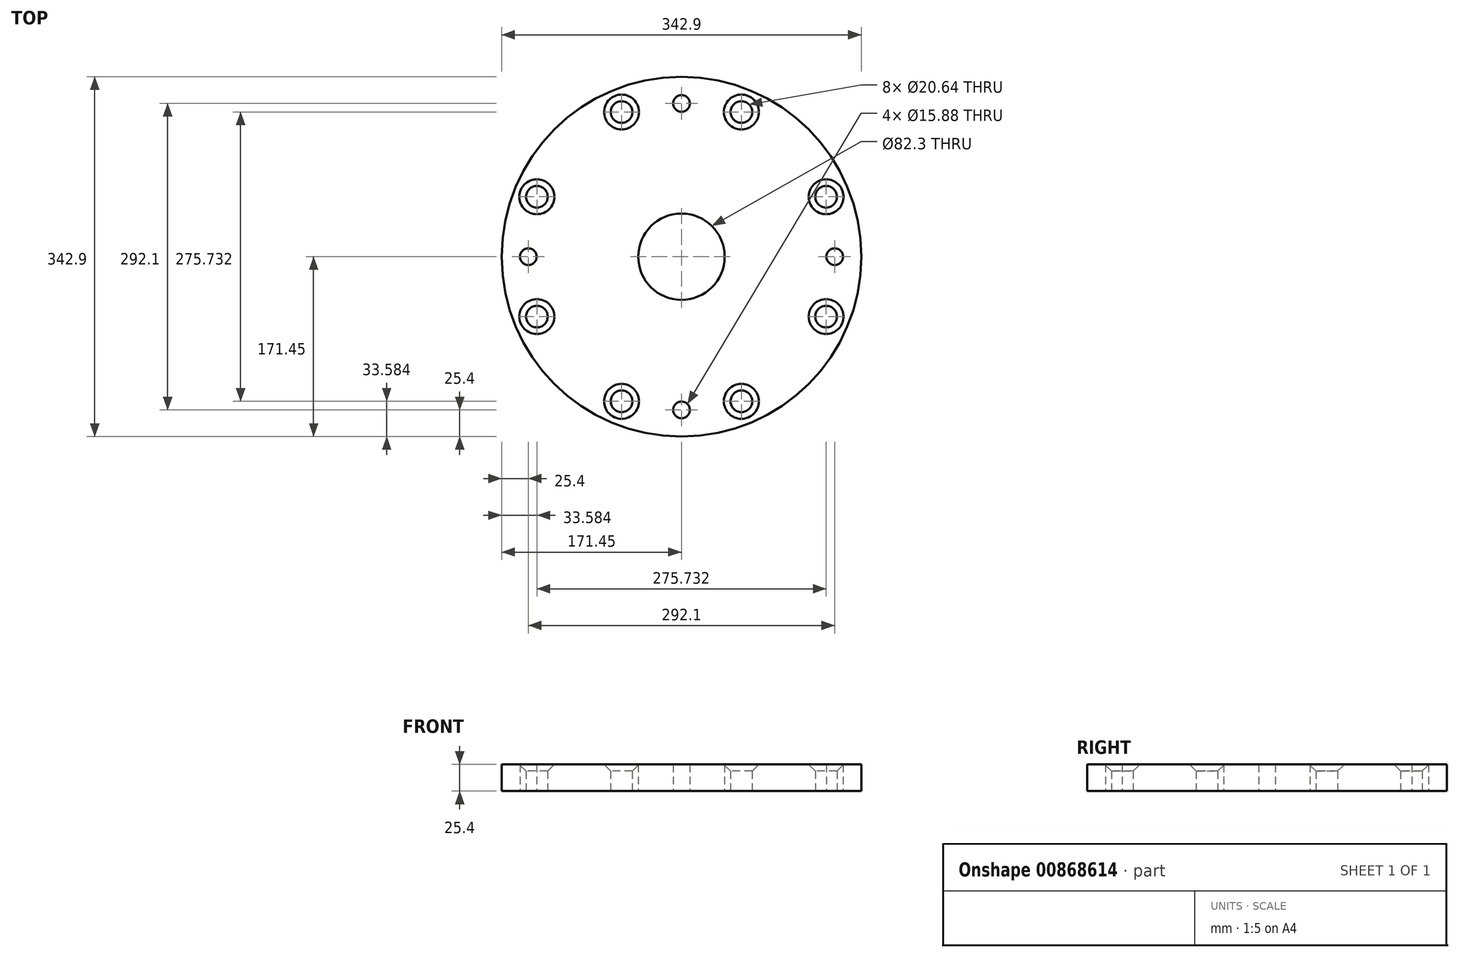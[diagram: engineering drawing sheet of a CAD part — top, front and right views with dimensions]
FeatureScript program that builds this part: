
annotation { "Feature Type Name" : "Feature", "Feature Type Description" : "" }
export const myFeature = defineFeature(function(context is Context, id is Id, definition is map)
    precondition{}
    {
        {
            var Q0;
            Q0=qCreatedBy(makeId("Top.planeOp"),FACE);
            var sketch = newSketch(context, id + "F0", { "sketchPlane" : qUnion([Q0])});
            skCircle(sketch, "E0", {"center": v(0, 0) * mm, "radius": 171.45 * mm});
            skCircle(sketch, "E1", {"center": v(0, 0) * mm, "radius": 146.05 * mm});
            skCircle(sketch, "E2", {"center": v(-146.05, 0) * mm, "radius": 7.94 * mm});
            skCircle(sketch, "E3", {"center": v(146.05, 0) * mm, "radius": 7.94 * mm});
            skCircle(sketch, "E4", {"center": v(0, 146.05) * mm, "radius": 7.94 * mm});
            skCircle(sketch, "E5", {"center": v(0, -146.05) * mm, "radius": 7.94 * mm});
            skCircle(sketch, "E6", {"center": v(0, 0) * mm, "radius": 149.23 * mm});
            skLineSegment(sketch, "E7", {"start": v(0, 0) * mm, "end": v(239, 0) * mm});
            skLineSegment(sketch, "E8", {"start": v(0, 0) * mm, "end": v(224.7, 93.07) * mm});
            skLineSegment(sketch, "E9", {"start": v(0, 0) * mm, "end": v(82.7, 199.64) * mm});
            skLineSegment(sketch, "E10.MirrorCS", {"start": v(0, 0) * mm, "end": v(-82.7, 199.64) * mm});
            skLineSegment(sketch, "E11.MirrorCS", {"start": v(0, 0) * mm, "end": v(-224.7, 93.07) * mm});
            skLineSegment(sketch, "E12.MirrorCS", {"start": v(0, 0) * mm, "end": v(224.7, -93.07) * mm});
            skLineSegment(sketch, "E13.MirrorCS", {"start": v(0, 0) * mm, "end": v(82.7, -199.64) * mm});
            skLineSegment(sketch, "E14.MirrorCS", {"start": v(0, 0) * mm, "end": v(-82.7, -199.64) * mm});
            skLineSegment(sketch, "E15.MirrorCS", {"start": v(0, 0) * mm, "end": v(-224.7, -93.07) * mm});
            skCircle(sketch, "E16", {"center": v(137.87, 57.1) * mm, "radius": 10.32 * mm});
            skCircle(sketch, "E17", {"center": v(57.1, 137.87) * mm, "radius": 10.32 * mm});
            skCircle(sketch, "E18", {"center": v(-57.1, 137.87) * mm, "radius": 10.32 * mm});
            skCircle(sketch, "E19", {"center": v(-137.87, 57.1) * mm, "radius": 10.32 * mm});
            skCircle(sketch, "E20", {"center": v(137.87, -57.1) * mm, "radius": 10.32 * mm});
            skCircle(sketch, "E21", {"center": v(57.1, -137.87) * mm, "radius": 10.32 * mm});
            skCircle(sketch, "E22", {"center": v(-57.1, -137.87) * mm, "radius": 10.32 * mm});
            skCircle(sketch, "E23", {"center": v(-137.87, -57.1) * mm, "radius": 10.32 * mm});
            skCircle(sketch, "E24", {"center": v(0, 0) * mm, "radius": 41.15 * mm});
            skSolve(sketch);
        }
        {
            var Q0;
            {var subQ1=sQuery(id+"F0.wireOp",EDGE,"E0");var subQ9=sQuery(id+"F0.wireOp",EDGE,"E8");var subQ10=makeQuery(id+"F0.imprint","INTERSECT",VERTEX,{"derivedFrom":[subQ1,subQ9]});Q0=makeQuery(id+"F0.imprint","IMPRINT",FACE,{"disambiguationData":[TD([[makeQuery(id+"F0.imprint","IMPRINT",EDGE,{"disambiguationData":[TD([[subQ10,1.0]])],"derivedFrom":subQ1}),1.0]])]});}
            var Q1;
            {var subQ1=sQuery(id+"F0.wireOp",EDGE,"E0");var subQ5=sQuery(id+"F0.wireOp",EDGE,"E8");var subQ6=makeQuery(id+"F0.imprint","INTERSECT",VERTEX,{"derivedFrom":[subQ1,subQ5]});Q1=makeQuery(id+"F0.imprint","IMPRINT",FACE,{"disambiguationData":[TD([[makeQuery(id+"F0.imprint","IMPRINT",EDGE,{"disambiguationData":[TD([[subQ6,-1.0]])],"derivedFrom":subQ1}),1.0]])]});}
            var Q2;
            {var subQ0=sQuery(id+"F0.wireOp",EDGE,"E10.MirrorCS");var subQ1=sQuery(id+"F0.wireOp",EDGE,"E0");var subQ2=makeQuery(id+"F0.imprint","INTERSECT",VERTEX,{"derivedFrom":[subQ1,subQ0]});Q2=makeQuery(id+"F0.imprint","IMPRINT",FACE,{"disambiguationData":[TD([[makeQuery(id+"F0.imprint","IMPRINT",EDGE,{"disambiguationData":[TD([[subQ2,-1.0]])],"derivedFrom":subQ1}),1.0]])]});}
            var Q3;
            {var subQ0=sQuery(id+"F0.wireOp",EDGE,"E13.MirrorCS");var subQ1=sQuery(id+"F0.wireOp",EDGE,"E0");var subQ2=makeQuery(id+"F0.imprint","INTERSECT",VERTEX,{"derivedFrom":[subQ1,subQ0]});Q3=makeQuery(id+"F0.imprint","IMPRINT",FACE,{"disambiguationData":[TD([[makeQuery(id+"F0.imprint","IMPRINT",EDGE,{"disambiguationData":[TD([[subQ2,-1.0]])],"derivedFrom":subQ1}),1.0]])]});}
            var Q4;
            {var subQ5=sQuery(id+"F0.wireOp",EDGE,"E7");var subQ8=sQuery(id+"F0.wireOp",EDGE,"E0");var subQ11=makeQuery(id+"F0.imprint","INTERSECT",VERTEX,{"derivedFrom":[subQ8,subQ5]});Q4=makeQuery(id+"F0.imprint","IMPRINT",FACE,{"disambiguationData":[TD([[makeQuery(id+"F0.imprint","IMPRINT",EDGE,{"disambiguationData":[TD([[subQ11,1.0]])],"derivedFrom":subQ8}),1.0]])]});}
            var Q5;
            {var subQ8=sQuery(id+"F0.wireOp",EDGE,"E9");var subQ9=sQuery(id+"F0.wireOp",EDGE,"E0");var subQ10=makeQuery(id+"F0.imprint","INTERSECT",VERTEX,{"derivedFrom":[subQ9,subQ8]});Q5=makeQuery(id+"F0.imprint","IMPRINT",FACE,{"disambiguationData":[TD([[makeQuery(id+"F0.imprint","IMPRINT",EDGE,{"disambiguationData":[TD([[subQ10,-1.0]])],"derivedFrom":subQ9}),1.0]])]});}
            var Q6;
            {var subQ5=sQuery(id+"F0.wireOp",EDGE,"E14.MirrorCS");var subQ6=sQuery(id+"F0.wireOp",EDGE,"E0");var subQ7=makeQuery(id+"F0.imprint","INTERSECT",VERTEX,{"derivedFrom":[subQ6,subQ5]});Q6=makeQuery(id+"F0.imprint","IMPRINT",FACE,{"disambiguationData":[TD([[makeQuery(id+"F0.imprint","IMPRINT",EDGE,{"disambiguationData":[TD([[subQ7,-1.0]])],"derivedFrom":subQ6}),1.0]])]});}
            var Q7;
            {var subQ8=sQuery(id+"F0.wireOp",EDGE,"E11.MirrorCS");var subQ9=sQuery(id+"F0.wireOp",EDGE,"E0");var subQ10=makeQuery(id+"F0.imprint","INTERSECT",VERTEX,{"derivedFrom":[subQ9,subQ8]});Q7=makeQuery(id+"F0.imprint","IMPRINT",FACE,{"disambiguationData":[TD([[makeQuery(id+"F0.imprint","IMPRINT",EDGE,{"disambiguationData":[TD([[subQ10,-1.0]])],"derivedFrom":subQ9}),1.0]])]});}
            var Q8;
            {var subQ3=sQuery(id+"F0.wireOp",EDGE,"E19");var subQ6=sQuery(id+"F0.wireOp",EDGE,"E1");var subQ13=makeQuery(id+"F0.imprint","INTERSECT",VERTEX,{"disambiguationData":[OD(1.0)],"derivedFrom":[subQ6,subQ3]});Q8=makeQuery(id+"F0.imprint","IMPRINT",FACE,{"disambiguationData":[TD([[makeQuery(id+"F0.imprint","IMPRINT",EDGE,{"disambiguationData":[TD([[subQ13,-1.0]])],"derivedFrom":subQ6}),1.0]])]});}
            var Q9;
            {var subQ0=sQuery(id+"F0.wireOp",EDGE,"E18");var subQ1=sQuery(id+"F0.wireOp",EDGE,"E1");var subQ2=makeQuery(id+"F0.imprint","INTERSECT",VERTEX,{"disambiguationData":[OD(1.0)],"derivedFrom":[subQ1,subQ0]});Q9=makeQuery(id+"F0.imprint","IMPRINT",FACE,{"disambiguationData":[TD([[makeQuery(id+"F0.imprint","IMPRINT",EDGE,{"disambiguationData":[TD([[subQ2,-1.0]])],"derivedFrom":subQ1}),1.0]])]});}
            var Q10;
            {var subQ1=sQuery(id+"F0.wireOp",EDGE,"E1");var subQ12=sQuery(id+"F0.wireOp",EDGE,"E17");var subQ14=makeQuery(id+"F0.imprint","INTERSECT",VERTEX,{"disambiguationData":[OD(1.0)],"derivedFrom":[subQ1,subQ12]});Q10=makeQuery(id+"F0.imprint","IMPRINT",FACE,{"disambiguationData":[TD([[makeQuery(id+"F0.imprint","IMPRINT",EDGE,{"disambiguationData":[TD([[subQ14,-1.0]])],"derivedFrom":subQ1}),1.0]])]});}
            var Q11;
            {var subQ0=sQuery(id+"F0.wireOp",EDGE,"E16");var subQ1=sQuery(id+"F0.wireOp",EDGE,"E1");var subQ2=makeQuery(id+"F0.imprint","INTERSECT",VERTEX,{"disambiguationData":[OD(1.0)],"derivedFrom":[subQ1,subQ0]});Q11=makeQuery(id+"F0.imprint","IMPRINT",FACE,{"disambiguationData":[TD([[makeQuery(id+"F0.imprint","IMPRINT",EDGE,{"disambiguationData":[TD([[subQ2,-1.0]])],"derivedFrom":subQ1}),1.0]])]});}
            var Q12;
            {var subQ1=sQuery(id+"F0.wireOp",EDGE,"E3");var subQ5=sQuery(id+"F0.wireOp",EDGE,"E1");var subQ6=makeQuery(id+"F0.imprint","INTERSECT",VERTEX,{"disambiguationData":[OD(0.0)],"derivedFrom":[subQ5,subQ1]});Q12=makeQuery(id+"F0.imprint","IMPRINT",FACE,{"disambiguationData":[TD([[makeQuery(id+"F0.imprint","IMPRINT",EDGE,{"disambiguationData":[TD([[subQ6,-1.0]])],"derivedFrom":subQ5}),1.0]])]});}
            var Q13;
            {var subQ3=sQuery(id+"F0.wireOp",EDGE,"E20");var subQ9=sQuery(id+"F0.wireOp",EDGE,"E1");var subQ11=makeQuery(id+"F0.imprint","INTERSECT",VERTEX,{"disambiguationData":[OD(1.0)],"derivedFrom":[subQ9,subQ3]});Q13=makeQuery(id+"F0.imprint","IMPRINT",FACE,{"disambiguationData":[TD([[makeQuery(id+"F0.imprint","IMPRINT",EDGE,{"disambiguationData":[TD([[subQ11,-1.0]])],"derivedFrom":subQ9}),1.0]])]});}
            var Q14;
            {var subQ1=sQuery(id+"F0.wireOp",EDGE,"E1");var subQ8=sQuery(id+"F0.wireOp",EDGE,"E21");var subQ11=makeQuery(id+"F0.imprint","INTERSECT",VERTEX,{"disambiguationData":[OD(1.0)],"derivedFrom":[subQ1,subQ8]});Q14=makeQuery(id+"F0.imprint","IMPRINT",FACE,{"disambiguationData":[TD([[makeQuery(id+"F0.imprint","IMPRINT",EDGE,{"disambiguationData":[TD([[subQ11,-1.0]])],"derivedFrom":subQ1}),1.0]])]});}
            var Q15;
            {var subQ6=sQuery(id+"F0.wireOp",EDGE,"E1");var subQ10=sQuery(id+"F0.wireOp",EDGE,"E22");var subQ11=makeQuery(id+"F0.imprint","INTERSECT",VERTEX,{"disambiguationData":[OD(1.0)],"derivedFrom":[subQ6,subQ10]});Q15=makeQuery(id+"F0.imprint","IMPRINT",FACE,{"disambiguationData":[TD([[makeQuery(id+"F0.imprint","IMPRINT",EDGE,{"disambiguationData":[TD([[subQ11,-1.0]])],"derivedFrom":subQ6}),1.0]])]});}
            var Q16;
            {var subQ1=sQuery(id+"F0.wireOp",EDGE,"E1");var subQ5=sQuery(id+"F0.wireOp",EDGE,"E23");var subQ6=makeQuery(id+"F0.imprint","INTERSECT",VERTEX,{"disambiguationData":[OD(1.0)],"derivedFrom":[subQ1,subQ5]});Q16=makeQuery(id+"F0.imprint","IMPRINT",FACE,{"disambiguationData":[TD([[makeQuery(id+"F0.imprint","IMPRINT",EDGE,{"disambiguationData":[TD([[subQ6,-1.0]])],"derivedFrom":subQ1}),1.0]])]});}
            var Q17;
            {var subQ0=sQuery(id+"F0.wireOp",EDGE,"E2");var subQ1=sQuery(id+"F0.wireOp",EDGE,"E1");var subQ2=makeQuery(id+"F0.imprint","INTERSECT",VERTEX,{"disambiguationData":[OD(1.0)],"derivedFrom":[subQ1,subQ0]});Q17=makeQuery(id+"F0.imprint","IMPRINT",FACE,{"disambiguationData":[TD([[makeQuery(id+"F0.imprint","IMPRINT",EDGE,{"disambiguationData":[TD([[subQ2,-1.0]])],"derivedFrom":subQ1}),-1.0]])]});}
            var Q18;
            {var subQ0=sQuery(id+"F0.wireOp",EDGE,"E19");var subQ1=sQuery(id+"F0.wireOp",EDGE,"E1");var subQ2=makeQuery(id+"F0.imprint","INTERSECT",VERTEX,{"disambiguationData":[OD(1.0)],"derivedFrom":[subQ1,subQ0]});Q18=makeQuery(id+"F0.imprint","IMPRINT",FACE,{"disambiguationData":[TD([[makeQuery(id+"F0.imprint","IMPRINT",EDGE,{"disambiguationData":[TD([[subQ2,-1.0]])],"derivedFrom":subQ1}),-1.0]])]});}
            var Q19;
            {var subQ0=sQuery(id+"F0.wireOp",EDGE,"E15.MirrorCS");var subQ1=sQuery(id+"F0.wireOp",EDGE,"E0");var subQ2=makeQuery(id+"F0.imprint","INTERSECT",VERTEX,{"derivedFrom":[subQ1,subQ0]});Q19=makeQuery(id+"F0.imprint","IMPRINT",FACE,{"disambiguationData":[TD([[makeQuery(id+"F0.imprint","IMPRINT",EDGE,{"disambiguationData":[TD([[subQ2,-1.0]])],"derivedFrom":subQ1}),1.0]])]});}
            var Q20;
            {var subQ0=sQuery(id+"F0.wireOp",EDGE,"E23");var subQ1=sQuery(id+"F0.wireOp",EDGE,"E1");var subQ2=makeQuery(id+"F0.imprint","INTERSECT",VERTEX,{"disambiguationData":[OD(1.0)],"derivedFrom":[subQ1,subQ0]});Q20=makeQuery(id+"F0.imprint","IMPRINT",FACE,{"disambiguationData":[TD([[makeQuery(id+"F0.imprint","IMPRINT",EDGE,{"disambiguationData":[TD([[subQ2,-1.0]])],"derivedFrom":subQ1}),-1.0]])]});}
            var Q21;
            {var subQ0=sQuery(id+"F0.wireOp",EDGE,"E22");var subQ1=sQuery(id+"F0.wireOp",EDGE,"E1");var subQ2=makeQuery(id+"F0.imprint","INTERSECT",VERTEX,{"disambiguationData":[OD(1.0)],"derivedFrom":[subQ1,subQ0]});Q21=makeQuery(id+"F0.imprint","IMPRINT",FACE,{"disambiguationData":[TD([[makeQuery(id+"F0.imprint","IMPRINT",EDGE,{"disambiguationData":[TD([[subQ2,-1.0]])],"derivedFrom":subQ1}),-1.0]])]});}
            var Q22;
            {var subQ0=sQuery(id+"F0.wireOp",EDGE,"E5");var subQ1=sQuery(id+"F0.wireOp",EDGE,"E1");var subQ2=makeQuery(id+"F0.imprint","INTERSECT",VERTEX,{"disambiguationData":[OD(1.0)],"derivedFrom":[subQ1,subQ0]});Q22=makeQuery(id+"F0.imprint","IMPRINT",FACE,{"disambiguationData":[TD([[makeQuery(id+"F0.imprint","IMPRINT",EDGE,{"disambiguationData":[TD([[subQ2,-1.0]])],"derivedFrom":subQ1}),-1.0]])]});}
            var Q23;
            {var subQ0=sQuery(id+"F0.wireOp",EDGE,"E21");var subQ1=sQuery(id+"F0.wireOp",EDGE,"E1");var subQ2=makeQuery(id+"F0.imprint","INTERSECT",VERTEX,{"disambiguationData":[OD(1.0)],"derivedFrom":[subQ1,subQ0]});Q23=makeQuery(id+"F0.imprint","IMPRINT",FACE,{"disambiguationData":[TD([[makeQuery(id+"F0.imprint","IMPRINT",EDGE,{"disambiguationData":[TD([[subQ2,-1.0]])],"derivedFrom":subQ1}),-1.0]])]});}
            var Q24;
            {var subQ0=sQuery(id+"F0.wireOp",EDGE,"E20");var subQ1=sQuery(id+"F0.wireOp",EDGE,"E1");var subQ2=makeQuery(id+"F0.imprint","INTERSECT",VERTEX,{"disambiguationData":[OD(1.0)],"derivedFrom":[subQ1,subQ0]});Q24=makeQuery(id+"F0.imprint","IMPRINT",FACE,{"disambiguationData":[TD([[makeQuery(id+"F0.imprint","IMPRINT",EDGE,{"disambiguationData":[TD([[subQ2,-1.0]])],"derivedFrom":subQ1}),-1.0]])]});}
            var Q25;
            {var subQ0=sQuery(id+"F0.wireOp",EDGE,"E3");var subQ1=sQuery(id+"F0.wireOp",EDGE,"E1");var subQ2=makeQuery(id+"F0.imprint","INTERSECT",VERTEX,{"disambiguationData":[OD(0.0)],"derivedFrom":[subQ1,subQ0]});Q25=makeQuery(id+"F0.imprint","IMPRINT",FACE,{"disambiguationData":[TD([[makeQuery(id+"F0.imprint","IMPRINT",EDGE,{"disambiguationData":[TD([[subQ2,-1.0]])],"derivedFrom":subQ1}),-1.0]])]});}
            var Q26;
            {var subQ0=sQuery(id+"F0.wireOp",EDGE,"E16");var subQ1=sQuery(id+"F0.wireOp",EDGE,"E1");var subQ2=makeQuery(id+"F0.imprint","INTERSECT",VERTEX,{"disambiguationData":[OD(1.0)],"derivedFrom":[subQ1,subQ0]});Q26=makeQuery(id+"F0.imprint","IMPRINT",FACE,{"disambiguationData":[TD([[makeQuery(id+"F0.imprint","IMPRINT",EDGE,{"disambiguationData":[TD([[subQ2,-1.0]])],"derivedFrom":subQ1}),-1.0]])]});}
            var Q27;
            {var subQ0=sQuery(id+"F0.wireOp",EDGE,"E17");var subQ1=sQuery(id+"F0.wireOp",EDGE,"E1");var subQ2=makeQuery(id+"F0.imprint","INTERSECT",VERTEX,{"disambiguationData":[OD(1.0)],"derivedFrom":[subQ1,subQ0]});Q27=makeQuery(id+"F0.imprint","IMPRINT",FACE,{"disambiguationData":[TD([[makeQuery(id+"F0.imprint","IMPRINT",EDGE,{"disambiguationData":[TD([[subQ2,-1.0]])],"derivedFrom":subQ1}),-1.0]])]});}
            var Q28;
            {var subQ0=sQuery(id+"F0.wireOp",EDGE,"E4");var subQ1=sQuery(id+"F0.wireOp",EDGE,"E1");var subQ2=makeQuery(id+"F0.imprint","INTERSECT",VERTEX,{"disambiguationData":[OD(1.0)],"derivedFrom":[subQ1,subQ0]});Q28=makeQuery(id+"F0.imprint","IMPRINT",FACE,{"disambiguationData":[TD([[makeQuery(id+"F0.imprint","IMPRINT",EDGE,{"disambiguationData":[TD([[subQ2,-1.0]])],"derivedFrom":subQ1}),-1.0]])]});}
            var Q29;
            {var subQ0=sQuery(id+"F0.wireOp",EDGE,"E18");var subQ1=sQuery(id+"F0.wireOp",EDGE,"E1");var subQ2=makeQuery(id+"F0.imprint","INTERSECT",VERTEX,{"disambiguationData":[OD(1.0)],"derivedFrom":[subQ1,subQ0]});Q29=makeQuery(id+"F0.imprint","IMPRINT",FACE,{"disambiguationData":[TD([[makeQuery(id+"F0.imprint","IMPRINT",EDGE,{"disambiguationData":[TD([[subQ2,-1.0]])],"derivedFrom":subQ1}),-1.0]])]});}
            extrude(context, id + "F1", {"entities" : qUnion([Q0, Q1, Q2, Q3, Q4, Q5, Q6, Q7, Q8, Q9, Q10, Q11, Q12, Q13, Q14, Q15, Q16, Q17, Q18, Q19, Q20, Q21, Q22, Q23, Q24, Q25, Q26, Q27, Q28, Q29]), "depth" : 25.4 * mm, "offsetDistance" : 25.4 * mm});
        }
        {
            var Q0;
            Q0=makeQuery(id+"F1.opExtrude","CAP_EDGE",EDGE,{"disambiguationData":[OSD([sQuery(id+"F0.wireOp",EDGE,"E18")])],"isStart":false});
            var Q1;
            Q1=makeQuery(id+"F1.opExtrude","CAP_EDGE",EDGE,{"disambiguationData":[OSD([sQuery(id+"F0.wireOp",EDGE,"E17")])],"isStart":false});
            var Q2;
            Q2=makeQuery(id+"F1.opExtrude","CAP_EDGE",EDGE,{"disambiguationData":[OSD([sQuery(id+"F0.wireOp",EDGE,"E16")])],"isStart":false});
            var Q3;
            Q3=makeQuery(id+"F1.opExtrude","CAP_EDGE",EDGE,{"disambiguationData":[OSD([sQuery(id+"F0.wireOp",EDGE,"E20")])],"isStart":false});
            var Q4;
            Q4=makeQuery(id+"F1.opExtrude","CAP_EDGE",EDGE,{"disambiguationData":[OSD([sQuery(id+"F0.wireOp",EDGE,"E22")])],"isStart":false});
            var Q5;
            Q5=makeQuery(id+"F1.opExtrude","CAP_EDGE",EDGE,{"disambiguationData":[OSD([sQuery(id+"F0.wireOp",EDGE,"E23")])],"isStart":false});
            var Q6;
            Q6=makeQuery(id+"F1.opExtrude","CAP_EDGE",EDGE,{"disambiguationData":[OSD([sQuery(id+"F0.wireOp",EDGE,"E19")])],"isStart":false});
            var Q7;
            Q7=makeQuery(id+"F1.opExtrude","CAP_EDGE",EDGE,{"disambiguationData":[OSD([sQuery(id+"F0.wireOp",EDGE,"E21")])],"isStart":false});
            chamfer(context, id + "F2", {"entities" : qUnion([Q0, Q1, Q2, Q3, Q4, Q5, Q6, Q7]), "width" : 6.35 * mm, "tangentPropagation" : true});
        }
    });
